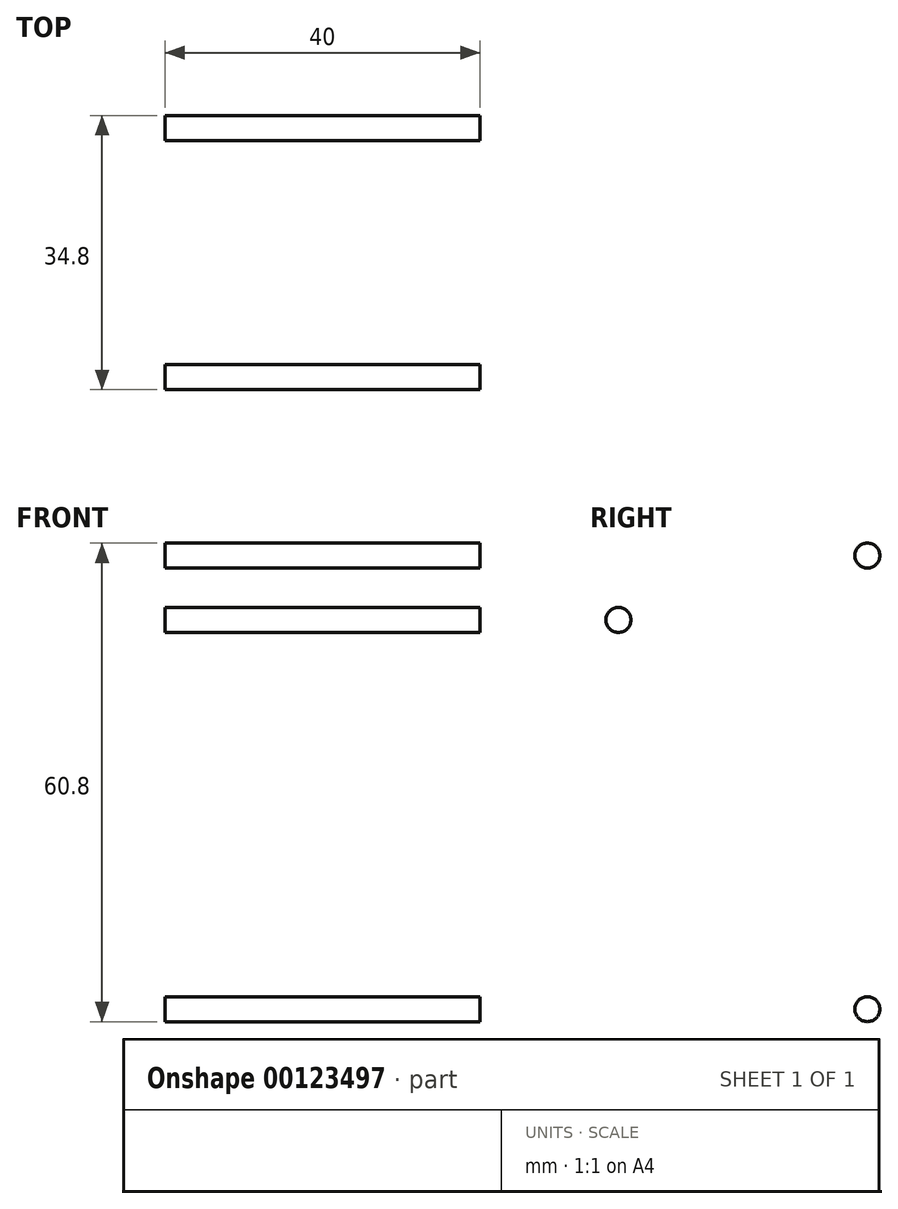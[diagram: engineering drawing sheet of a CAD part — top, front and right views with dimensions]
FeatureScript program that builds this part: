
annotation { "Feature Type Name" : "Feature", "Feature Type Description" : "" }
export const myFeature = defineFeature(function(context is Context, id is Id, definition is map)
    precondition{}
    {
        {
            var Q0;
            Q0=qCreatedBy(makeId("Right.planeOp"),FACE);
            var sketch = newSketch(context, id + "F0", { "sketchPlane" : qUnion([Q0])});
            skCircle(sketch, "E0", {"center": v(0, 0) * mm, "radius": 1.59 * mm});
            skCircle(sketch, "E1", {"center": v(-31.62, 49.45) * mm, "radius": 1.59 * mm});
            skCircle(sketch, "E2", {"center": v(0, 57.62) * mm, "radius": 1.59 * mm});
            skSolve(sketch);
        }
        {
            var Q0;
            Q0=makeQuery(id+"F0.imprint","IMPRINT",FACE,{"disambiguationData":[TD([[makeQuery(id+"F0.imprint","IMPRINT",EDGE,{"derivedFrom":sQuery(id+"F0.wireOp",EDGE,"E0")}),1.0]])]});
            extrude(context, id + "F1", {"entities" : qUnion([Q0]), "depth" : 40 * mm});
        }
        {
            var Q0;
            Q0=makeQuery(id+"F0.imprint","IMPRINT",FACE,{"disambiguationData":[TD([[makeQuery(id+"F0.imprint","IMPRINT",EDGE,{"derivedFrom":sQuery(id+"F0.wireOp",EDGE,"E1")}),1.0]])]});
            var Q1;
            Q1=makeQuery(id+"F0.imprint","IMPRINT",FACE,{"disambiguationData":[TD([[makeQuery(id+"F0.imprint","IMPRINT",EDGE,{"derivedFrom":sQuery(id+"F0.wireOp",EDGE,"E2")}),1.0]])]});
            extrude(context, id + "F2", {"entities" : qUnion([Q0, Q1]), "depth" : 40 * mm});
        }
    });
